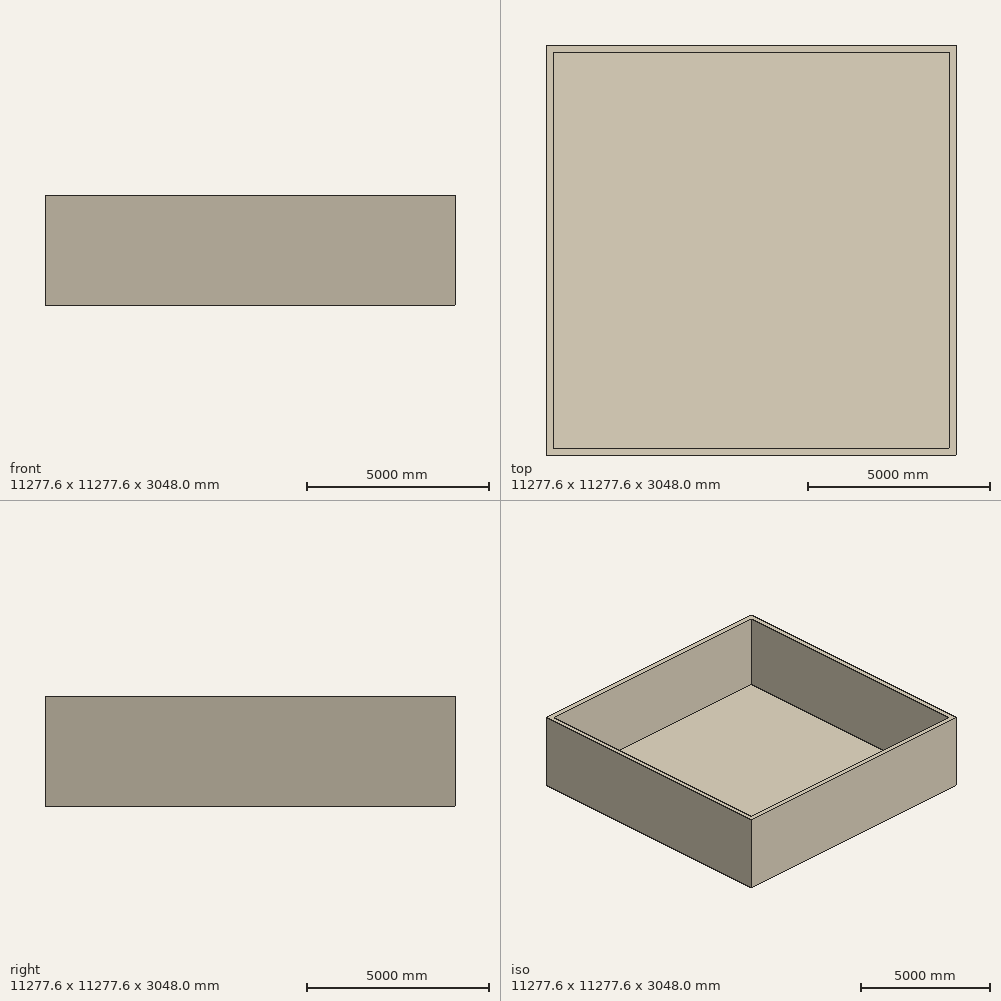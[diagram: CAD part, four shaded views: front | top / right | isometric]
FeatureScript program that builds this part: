
annotation { "Feature Type Name" : "Feature", "Feature Type Description" : "" }
export const myFeature = defineFeature(function(context is Context, id is Id, definition is map)
    precondition{}
    {
        {
            var Q0;
            Q0=qCreatedBy(makeId("Top.planeOp"),FACE);
            var sketch = newSketch(context, id + "F0", { "sketchPlane" : qUnion([Q0])});
            skLineSegment(sketch, "E0.bottom", {"start": v(-5638.8, 5638.8) * mm, "end": v(5638.8, 5638.8) * mm});
            skLineSegment(sketch, "E0.top", {"start": v(-5638.8, -5638.8) * mm, "end": v(5638.8, -5638.8) * mm});
            skLineSegment(sketch, "E0.left", {"start": v(-5638.8, 5638.8) * mm, "end": v(-5638.8, -5638.8) * mm});
            skLineSegment(sketch, "E0.right", {"start": v(5638.8, 5638.8) * mm, "end": v(5638.8, -5638.8) * mm});
            skSolve(sketch);
        }
        {
            var Q0;
            Q0 = qSketchRegion(id + "F0", true);
            extrude(context, id + "F1", {"entities" : qUnion([Q0]), "depth" : 3048 * mm, "offsetDistance" : 25.4 * mm});
        }
        {
            var Q0;
            Q0=makeQuery(id+"F1.opExtrude","CAP_FACE",FACE,{"disambiguationData":[OSD([sQuery(id+"F0.wireOp",EDGE,"E0.bottom"),sQuery(id+"F0.wireOp",EDGE,"E0.top"),sQuery(id+"F0.wireOp",EDGE,"E0.left"),sQuery(id+"F0.wireOp",EDGE,"E0.right")])],"isStart":false});
            var sketch = newSketch(context, id + "F2", { "sketchPlane" : qUnion([Q0])});
            skLineSegment(sketch, "E1.bottom", {"start": v(-5435.6, -5435.6) * mm, "end": v(5435.6, -5435.6) * mm});
            skLineSegment(sketch, "E1.top", {"start": v(-5435.6, 5435.6) * mm, "end": v(5435.6, 5435.6) * mm});
            skLineSegment(sketch, "E1.left", {"start": v(-5435.6, -5435.6) * mm, "end": v(-5435.6, 5435.6) * mm});
            skLineSegment(sketch, "E1.right", {"start": v(5435.6, -5435.6) * mm, "end": v(5435.6, 5435.6) * mm});
            skPoint(sketch, "E1.middle", {"position": v(0, 0) * mm});
            skSolve(sketch);
        }
        {
            var Q0;
            Q0 = qSketchRegion(id + "F2", true);
            extrude(context, id + "F3", {"entities" : qUnion([Q0]), "operationType" : NewBodyOperationType.REMOVE, "oppositeDirection" : true, "depth" : 2946.4 * mm, "offsetDistance" : 25.4 * mm});
        }
    });
